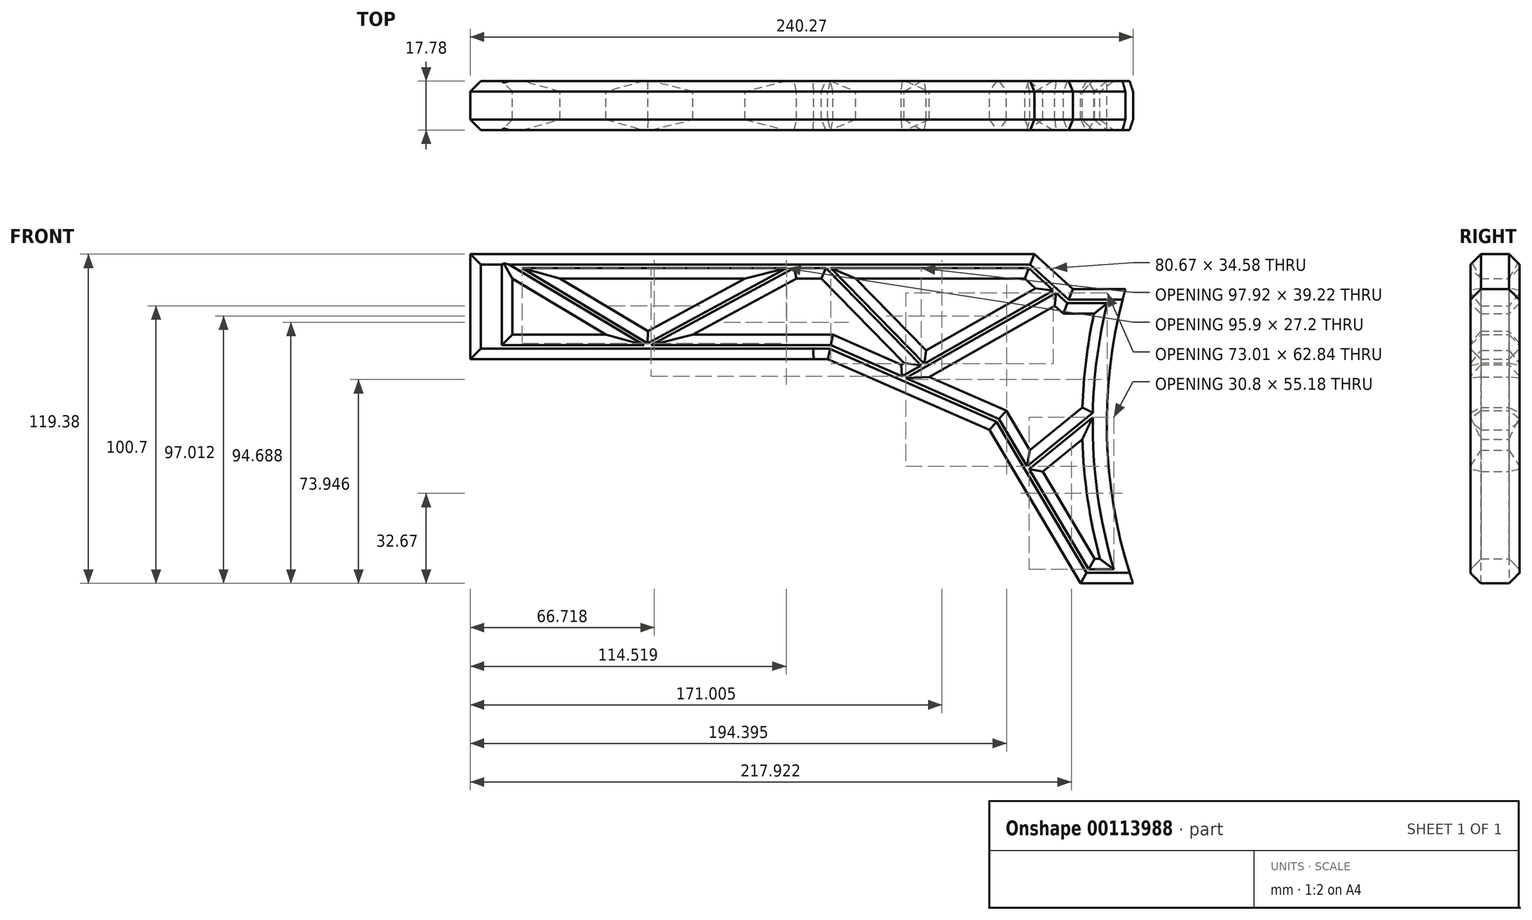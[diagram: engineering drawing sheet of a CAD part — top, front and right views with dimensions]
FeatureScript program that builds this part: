
annotation { "Feature Type Name" : "Feature", "Feature Type Description" : "" }
export const myFeature = defineFeature(function(context is Context, id is Id, definition is map)
    precondition{}
    {
        {
            var Q0;
            Q0=qCreatedBy(makeId("Front.planeOp"),FACE);
            var sketch = newSketch(context, id + "F0", { "sketchPlane" : qUnion([Q0])});
            skLineSegment(sketch, "E0", {"start": v(16.5, 0) * mm, "end": v(146.11, 0) * mm});
            skLineSegment(sketch, "E1", {"start": v(16.5, 38.1) * mm, "end": v(220.98, 38.1) * mm});
            skPoint(sketch, "E2.third.point", {"position": v(702.6, 206.51) * mm});
            skLineSegment(sketch, "E3", {"start": v(106.48, -51.1) * mm, "end": v(103.94, -51.1) * mm});
            skLineSegment(sketch, "E4.trimOffspring", {"start": v(-124.11, 15.8) * mm, "end": v(-124.11, 15.18) * mm, "construction": true});
            skLineSegment(sketch, "E5", {"start": v(220.98, 38.1) * mm, "end": v(234.95, 25.4) * mm});
            skLineSegment(sketch, "E6", {"start": v(234.95, 25.4) * mm, "end": v(254, 25.4) * mm});
            skLineSegment(sketch, "E7", {"start": v(256.78, -81.28) * mm, "end": v(237.73, -81.28) * mm});
            skArc(sketch, "E8", {"start": v(146.11, 0) * mm, "mid": v(143.53, 0.04) * mm, "end": v(140.94, 0) * mm});
            skLineSegment(sketch, "E9", {"start": v(237.73, -81.28) * mm, "end": v(204.68, -25.64) * mm});
            skLineSegment(sketch, "E10", {"start": v(204.68, -25.64) * mm, "end": v(146.11, 0) * mm});
            skArc(sketch, "E11", {"start": v(254, 25.4) * mm, "mid": v(247.3, -28.15) * mm, "end": v(256.78, -81.28) * mm});
            skLineSegment(sketch, "E12.2", {"start": v(31.75, 8.9) * mm, "end": v(48.98, 8.9) * mm});
            skLineSegment(sketch, "E12.3", {"start": v(217.54, 29.2) * mm, "end": v(221.4, 25.7) * mm});
            skLineSegment(sketch, "E12.4", {"start": v(210.86, -18.65) * mm, "end": v(182.89, -6.4) * mm});
            skLineSegment(sketch, "E12.5", {"start": v(242.79, -72.4) * mm, "end": v(223.99, -40.74) * mm});
            skArc(sketch, "E12.6", {"start": v(242.62, 16.5) * mm, "mid": v(239.75, -0.4) * mm, "end": v(238.43, -17.5) * mm});
            skLineSegment(sketch, "E12.7", {"start": v(231.51, 16.5) * mm, "end": v(242.62, 16.5) * mm});
            skLineSegment(sketch, "E13", {"start": v(242.79, -72.4) * mm, "end": v(244.8, -72.4) * mm});
            skLineSegment(sketch, "E14", {"start": v(219.4, -33.01) * mm, "end": v(238.43, -17.5) * mm});
            skLineSegment(sketch, "E15", {"start": v(223.99, -40.74) * mm, "end": v(238.42, -28.98) * mm});
            skLineSegment(sketch, "E16.trimOffspring", {"start": v(219.4, -33.01) * mm, "end": v(210.86, -18.65) * mm});
            skArc(sketch, "E17.trimOffspring", {"start": v(238.42, -28.98) * mm, "mid": v(240.34, -50.87) * mm, "end": v(244.8, -72.39) * mm});
            skLineSegment(sketch, "E18", {"start": v(221.4, 25.7) * mm, "end": v(181.8, 3.2) * mm});
            skLineSegment(sketch, "E19", {"start": v(182.89, -6.4) * mm, "end": v(228.32, 19.41) * mm});
            skLineSegment(sketch, "E20", {"start": v(173.8, -1.34) * mm, "end": v(143.8, 29.2) * mm});
            skLineSegment(sketch, "E21", {"start": v(156.26, 29.21) * mm, "end": v(181.8, 3.2) * mm});
            skLineSegment(sketch, "E22.trimOffspring", {"start": v(173.8, -1.34) * mm, "end": v(172.73, -1.95) * mm});
            skLineSegment(sketch, "E23.trimOffspring", {"start": v(172.73, -1.95) * mm, "end": v(147.98, 8.9) * mm});
            skLineSegment(sketch, "E24.trimOffspring", {"start": v(228.32, 19.41) * mm, "end": v(231.51, 16.5) * mm});
            skLineSegment(sketch, "E25.trimOffspring", {"start": v(156.26, 29.2) * mm, "end": v(217.54, 29.2) * mm});
            skLineSegment(sketch, "E26", {"start": v(134.82, 29.2) * mm, "end": v(97.15, 8.89) * mm});
            skLineSegment(sketch, "E27", {"start": v(80.86, 10.2) * mm, "end": v(116.1, 29.2) * mm});
            skLineSegment(sketch, "E28.trimOffspring", {"start": v(49.07, 29.2) * mm, "end": v(116.1, 29.2) * mm});
            skLineSegment(sketch, "E29.trimOffspring", {"start": v(134.82, 29.2) * mm, "end": v(143.8, 29.2) * mm});
            skLineSegment(sketch, "E30.trimOffspring", {"start": v(97.15, 8.9) * mm, "end": v(147.98, 8.9) * mm});
            skLineSegment(sketch, "E31", {"start": v(16.51, 29.21) * mm, "end": v(16.51, 8.9) * mm});
            skPoint(sketch, "E32.orphan", {"position": v(8.9, 8.9) * mm});
            skPoint(sketch, "E12.1.start.orphan", {"position": v(8.9, 29.21) * mm});
            skLineSegment(sketch, "E33", {"start": v(16.5, 38.1) * mm, "end": v(16.5, 0) * mm});
            skPoint(sketch, "E34.start.orphan", {"position": v(0, 38.1) * mm});
            skPoint(sketch, "E35.orphan", {"position": v(0, 0) * mm});
            skLineSegment(sketch, "E36", {"start": v(48.98, 8.89) * mm, "end": v(65.73, 8.89) * mm});
            skLineSegment(sketch, "E37", {"start": v(31.75, 29.21) * mm, "end": v(31.75, 8.9) * mm});
            skLineSegment(sketch, "E38", {"start": v(31.75, 29.21) * mm, "end": v(65.73, 8.89) * mm});
            skLineSegment(sketch, "E39", {"start": v(49.07, 29.2) * mm, "end": v(80.86, 10.2) * mm});
            skPoint(sketch, "E40.end.orphan", {"position": v(33.27, 29.2) * mm});
            skPoint(sketch, "E41.orphan", {"position": v(78.43, 8.9) * mm});
            skSolve(sketch);
        }
        {
            var Q0;
            Q0=makeQuery(id+"F0.imprint","IMPRINT",FACE,{"disambiguationData":[TD([[makeQuery(id+"F0.imprint","IMPRINT",EDGE,{"derivedFrom":sQuery(id+"F0.wireOp",EDGE,"E1")}),-1.0]])]});
            extrude(context, id + "F1", {"entities" : qUnion([Q0]), "depth" : 17.78 * mm});
        }
        {
            var Q0;
            Q0=makeQuery(id+"F1.opExtrude","CAP_EDGE",EDGE,{"disambiguationData":[OSD([sQuery(id+"F0.wireOp",EDGE,"E8")])],"isStart":false});
            var Q1;
            Q1=makeQuery(id+"F1.opExtrude","CAP_EDGE",EDGE,{"disambiguationData":[OSD([sQuery(id+"F0.wireOp",EDGE,"E10")])],"isStart":false});
            var Q2;
            Q2=makeQuery(id+"F1.opExtrude","CAP_EDGE",EDGE,{"disambiguationData":[OSD([sQuery(id+"F0.wireOp",EDGE,"E9")])],"isStart":false});
            var Q3;
            Q3=makeQuery(id+"F1.opExtrude","CAP_EDGE",EDGE,{"disambiguationData":[OSD([sQuery(id+"F0.wireOp",EDGE,"E7")])],"isStart":false});
            var Q4;
            Q4=makeQuery(id+"F1.opExtrude","CAP_EDGE",EDGE,{"disambiguationData":[OSD([sQuery(id+"F0.wireOp",EDGE,"E17.trimOffspring")])],"isStart":false});
            var Q5;
            Q5=makeQuery(id+"F1.opExtrude","CAP_EDGE",EDGE,{"disambiguationData":[OSD([sQuery(id+"F0.wireOp",EDGE,"E12.5")])],"isStart":false});
            var Q6;
            Q6=makeQuery(id+"F1.opExtrude","CAP_EDGE",EDGE,{"disambiguationData":[OSD([sQuery(id+"F0.wireOp",EDGE,"E13")])],"isStart":false});
            var Q7;
            Q7=makeQuery(id+"F1.opExtrude","CAP_EDGE",EDGE,{"disambiguationData":[OSD([sQuery(id+"F0.wireOp",EDGE,"E15")])],"isStart":false});
            var Q8;
            Q8=makeQuery(id+"F1.opExtrude","CAP_EDGE",EDGE,{"disambiguationData":[OSD([sQuery(id+"F0.wireOp",EDGE,"E16.trimOffspring")])],"isStart":false});
            var Q9;
            Q9=makeQuery(id+"F1.opExtrude","CAP_EDGE",EDGE,{"disambiguationData":[OSD([sQuery(id+"F0.wireOp",EDGE,"E14")])],"isStart":false});
            var Q10;
            Q10=makeQuery(id+"F1.opExtrude","CAP_EDGE",EDGE,{"disambiguationData":[OSD([sQuery(id+"F0.wireOp",EDGE,"E12.6")])],"isStart":false});
            var Q11;
            Q11=makeQuery(id+"F1.opExtrude","CAP_EDGE",EDGE,{"disambiguationData":[OSD([sQuery(id+"F0.wireOp",EDGE,"E12.7")])],"isStart":false});
            var Q12;
            Q12=makeQuery(id+"F1.opExtrude","CAP_EDGE",EDGE,{"disambiguationData":[OSD([sQuery(id+"F0.wireOp",EDGE,"E24.trimOffspring")])],"isStart":false});
            var Q13;
            Q13=makeQuery(id+"F1.opExtrude","CAP_EDGE",EDGE,{"disambiguationData":[OSD([sQuery(id+"F0.wireOp",EDGE,"E19")])],"isStart":false});
            var Q14;
            Q14=makeQuery(id+"F1.opExtrude","CAP_EDGE",EDGE,{"disambiguationData":[OSD([sQuery(id+"F0.wireOp",EDGE,"E12.4")])],"isStart":false});
            var Q15;
            Q15=makeQuery(id+"F1.opExtrude","CAP_EDGE",EDGE,{"disambiguationData":[OSD([sQuery(id+"F0.wireOp",EDGE,"E12.3")])],"isStart":false});
            var Q16;
            Q16=makeQuery(id+"F1.opExtrude","CAP_EDGE",EDGE,{"disambiguationData":[OSD([sQuery(id+"F0.wireOp",EDGE,"E25.trimOffspring")])],"isStart":false});
            var Q17;
            Q17=makeQuery(id+"F1.opExtrude","CAP_EDGE",EDGE,{"disambiguationData":[OSD([sQuery(id+"F0.wireOp",EDGE,"E21")])],"isStart":false});
            var Q18;
            Q18=makeQuery(id+"F1.opExtrude","CAP_EDGE",EDGE,{"disambiguationData":[OSD([sQuery(id+"F0.wireOp",EDGE,"E18")])],"isStart":false});
            var Q19;
            Q19=makeQuery(id+"F1.opExtrude","CAP_EDGE",EDGE,{"disambiguationData":[OSD([sQuery(id+"F0.wireOp",EDGE,"E23.trimOffspring")])],"isStart":false});
            var Q20;
            Q20=makeQuery(id+"F1.opExtrude","CAP_EDGE",EDGE,{"disambiguationData":[OSD([sQuery(id+"F0.wireOp",EDGE,"E30.trimOffspring")])],"isStart":false});
            var Q21;
            Q21=makeQuery(id+"F1.opExtrude","CAP_EDGE",EDGE,{"disambiguationData":[OSD([sQuery(id+"F0.wireOp",EDGE,"E22.trimOffspring")])],"isStart":false});
            var Q22;
            Q22=makeQuery(id+"F1.opExtrude","CAP_EDGE",EDGE,{"disambiguationData":[OSD([sQuery(id+"F0.wireOp",EDGE,"E20")])],"isStart":false});
            var Q23;
            Q23=makeQuery(id+"F1.opExtrude","CAP_EDGE",EDGE,{"disambiguationData":[OSD([sQuery(id+"F0.wireOp",EDGE,"E29.trimOffspring")])],"isStart":false});
            var Q24;
            Q24=makeQuery(id+"F1.opExtrude","CAP_EDGE",EDGE,{"disambiguationData":[OSD([sQuery(id+"F0.wireOp",EDGE,"E26")])],"isStart":false});
            var Q25;
            Q25=makeQuery(id+"F1.opExtrude","CAP_EDGE",EDGE,{"disambiguationData":[OSD([sQuery(id+"F0.wireOp",EDGE,"8kjQfZER-0lHH-HhN7-aV4i-Qcd4DPzWzpJs")])],"isStart":false});
            var Q26;
            Q26=makeQuery(id+"F1.opExtrude","CAP_EDGE",EDGE,{"disambiguationData":[OSD([sQuery(id+"F0.wireOp",EDGE,"E28.trimOffspring")])],"isStart":false});
            var Q27;
            Q27=makeQuery(id+"F1.opExtrude","CAP_EDGE",EDGE,{"disambiguationData":[OSD([sQuery(id+"F0.wireOp",EDGE,"E27")])],"isStart":false});
            var Q28;
            Q28=makeQuery(id+"F1.opExtrude","CAP_EDGE",EDGE,{"disambiguationData":[OSD([sQuery(id+"F0.wireOp",EDGE,"9419f677-d06b-4c3d-bac2-6876a50477b4.trimOffspring")])],"isStart":false});
            var Q29;
            Q29=makeQuery(id+"F1.opExtrude","CAP_EDGE",EDGE,{"disambiguationData":[OSD([sQuery(id+"F0.wireOp",EDGE,"E12.2")])],"isStart":false});
            var Q30;
            Q30=makeQuery(id+"F1.opExtrude","CAP_EDGE",EDGE,{"disambiguationData":[OSD([sQuery(id+"F0.wireOp",EDGE,"G8ACPXqJ-KlJt-v5ie-DtNp-ziiiNlemSXnz")])],"isStart":false});
            var Q31;
            Q31=makeQuery(id+"F1.opExtrude","CAP_EDGE",EDGE,{"disambiguationData":[OSD([sQuery(id+"F0.wireOp",EDGE,"E31")])],"isStart":false});
            var Q32;
            Q32=makeQuery(id+"F1.opExtrude","CAP_EDGE",EDGE,{"disambiguationData":[OSD([sQuery(id+"F0.wireOp",EDGE,"E1")])],"isStart":false});
            var Q33;
            Q33=makeQuery(id+"F1.opExtrude","CAP_EDGE",EDGE,{"disambiguationData":[OSD([sQuery(id+"F0.wireOp",EDGE,"E5")])],"isStart":true});
            var Q34;
            Q34=makeQuery(id+"F1.opExtrude","CAP_EDGE",EDGE,{"disambiguationData":[OSD([sQuery(id+"F0.wireOp",EDGE,"E6")])],"isStart":false});
            var Q35;
            Q35=makeQuery(id+"F1.opExtrude","CAP_EDGE",EDGE,{"disambiguationData":[OSD([sQuery(id+"F0.wireOp",EDGE,"E5")])],"isStart":false});
            var Q36;
            Q36=makeQuery(id+"F1.opExtrude","CAP_EDGE",EDGE,{"disambiguationData":[OSD([sQuery(id+"F0.wireOp",EDGE,"E0")])],"isStart":false});
            var Q37;
            Q37=makeQuery(id+"F1.opExtrude","CAP_EDGE",EDGE,{"disambiguationData":[OSD([sQuery(id+"F0.wireOp",EDGE,"E12.2")])],"isStart":true});
            var Q38;
            Q38=makeQuery(id+"F1.opExtrude","CAP_EDGE",EDGE,{"disambiguationData":[OSD([sQuery(id+"F0.wireOp",EDGE,"G8ACPXqJ-KlJt-v5ie-DtNp-ziiiNlemSXnz")])],"isStart":true});
            var Q39;
            Q39=makeQuery(id+"F1.opExtrude","CAP_EDGE",EDGE,{"disambiguationData":[OSD([sQuery(id+"F0.wireOp",EDGE,"9419f677-d06b-4c3d-bac2-6876a50477b4.trimOffspring")])],"isStart":true});
            var Q40;
            Q40=makeQuery(id+"F1.opExtrude","CAP_EDGE",EDGE,{"disambiguationData":[OSD([sQuery(id+"F0.wireOp",EDGE,"8kjQfZER-0lHH-HhN7-aV4i-Qcd4DPzWzpJs")])],"isStart":true});
            var Q41;
            Q41=makeQuery(id+"F1.opExtrude","CAP_EDGE",EDGE,{"disambiguationData":[OSD([sQuery(id+"F0.wireOp",EDGE,"E27")])],"isStart":true});
            var Q42;
            Q42=makeQuery(id+"F1.opExtrude","CAP_EDGE",EDGE,{"disambiguationData":[OSD([sQuery(id+"F0.wireOp",EDGE,"E31")])],"isStart":true});
            var Q43;
            Q43=makeQuery(id+"F1.opExtrude","CAP_EDGE",EDGE,{"disambiguationData":[OSD([sQuery(id+"F0.wireOp",EDGE,"E29.trimOffspring")])],"isStart":true});
            var Q44;
            Q44=makeQuery(id+"F1.opExtrude","CAP_EDGE",EDGE,{"disambiguationData":[OSD([sQuery(id+"F0.wireOp",EDGE,"E26")])],"isStart":true});
            var Q45;
            Q45=makeQuery(id+"F1.opExtrude","CAP_EDGE",EDGE,{"disambiguationData":[OSD([sQuery(id+"F0.wireOp",EDGE,"E28.trimOffspring")])],"isStart":true});
            var Q46;
            Q46=makeQuery(id+"F1.opExtrude","CAP_EDGE",EDGE,{"disambiguationData":[OSD([sQuery(id+"F0.wireOp",EDGE,"E22.trimOffspring")])],"isStart":true});
            var Q47;
            Q47=makeQuery(id+"F1.opExtrude","CAP_EDGE",EDGE,{"disambiguationData":[OSD([sQuery(id+"F0.wireOp",EDGE,"E20")])],"isStart":true});
            var Q48;
            Q48=makeQuery(id+"F1.opExtrude","CAP_EDGE",EDGE,{"disambiguationData":[OSD([sQuery(id+"F0.wireOp",EDGE,"E23.trimOffspring")])],"isStart":true});
            var Q49;
            Q49=makeQuery(id+"F1.opExtrude","CAP_EDGE",EDGE,{"disambiguationData":[OSD([sQuery(id+"F0.wireOp",EDGE,"E18")])],"isStart":true});
            var Q50;
            Q50=makeQuery(id+"F1.opExtrude","CAP_EDGE",EDGE,{"disambiguationData":[OSD([sQuery(id+"F0.wireOp",EDGE,"E14")])],"isStart":true});
            var Q51;
            Q51=makeQuery(id+"F1.opExtrude","CAP_EDGE",EDGE,{"disambiguationData":[OSD([sQuery(id+"F0.wireOp",EDGE,"E30.trimOffspring")])],"isStart":true});
            var Q52;
            Q52=makeQuery(id+"F1.opExtrude","CAP_EDGE",EDGE,{"disambiguationData":[OSD([sQuery(id+"F0.wireOp",EDGE,"E12.4")])],"isStart":true});
            var Q53;
            Q53=makeQuery(id+"F1.opExtrude","CAP_EDGE",EDGE,{"disambiguationData":[OSD([sQuery(id+"F0.wireOp",EDGE,"E16.trimOffspring")])],"isStart":true});
            var Q54;
            Q54=makeQuery(id+"F1.opExtrude","CAP_EDGE",EDGE,{"disambiguationData":[OSD([sQuery(id+"F0.wireOp",EDGE,"E21")])],"isStart":true});
            var Q55;
            Q55=makeQuery(id+"F1.opExtrude","CAP_EDGE",EDGE,{"disambiguationData":[OSD([sQuery(id+"F0.wireOp",EDGE,"E12.3")])],"isStart":true});
            var Q56;
            Q56=makeQuery(id+"F1.opExtrude","CAP_EDGE",EDGE,{"disambiguationData":[OSD([sQuery(id+"F0.wireOp",EDGE,"E25.trimOffspring")])],"isStart":true});
            var Q57;
            Q57=makeQuery(id+"F1.opExtrude","CAP_EDGE",EDGE,{"disambiguationData":[OSD([sQuery(id+"F0.wireOp",EDGE,"E24.trimOffspring")])],"isStart":true});
            var Q58;
            Q58=makeQuery(id+"F1.opExtrude","CAP_EDGE",EDGE,{"disambiguationData":[OSD([sQuery(id+"F0.wireOp",EDGE,"E19")])],"isStart":true});
            var Q59;
            Q59=makeQuery(id+"F1.opExtrude","CAP_EDGE",EDGE,{"disambiguationData":[OSD([sQuery(id+"F0.wireOp",EDGE,"E12.7")])],"isStart":true});
            var Q60;
            Q60=makeQuery(id+"F1.opExtrude","CAP_EDGE",EDGE,{"disambiguationData":[OSD([sQuery(id+"F0.wireOp",EDGE,"E12.6")])],"isStart":true});
            var Q61;
            Q61=makeQuery(id+"F1.opExtrude","CAP_EDGE",EDGE,{"disambiguationData":[OSD([sQuery(id+"F0.wireOp",EDGE,"E17.trimOffspring")])],"isStart":true});
            var Q62;
            Q62=makeQuery(id+"F1.opExtrude","CAP_EDGE",EDGE,{"disambiguationData":[OSD([sQuery(id+"F0.wireOp",EDGE,"E15")])],"isStart":true});
            var Q63;
            Q63=makeQuery(id+"F1.opExtrude","CAP_EDGE",EDGE,{"disambiguationData":[OSD([sQuery(id+"F0.wireOp",EDGE,"E13")])],"isStart":true});
            var Q64;
            Q64=makeQuery(id+"F1.opExtrude","CAP_EDGE",EDGE,{"disambiguationData":[OSD([sQuery(id+"F0.wireOp",EDGE,"E12.5")])],"isStart":true});
            var Q65;
            Q65=makeQuery(id+"F1.opExtrude","CAP_EDGE",EDGE,{"disambiguationData":[OSD([sQuery(id+"F0.wireOp",EDGE,"E7")])],"isStart":true});
            var Q66;
            Q66=makeQuery(id+"F1.opExtrude","CAP_EDGE",EDGE,{"disambiguationData":[OSD([sQuery(id+"F0.wireOp",EDGE,"E9")])],"isStart":true});
            var Q67;
            Q67=makeQuery(id+"F1.opExtrude","CAP_EDGE",EDGE,{"disambiguationData":[OSD([sQuery(id+"F0.wireOp",EDGE,"E10")])],"isStart":true});
            var Q68;
            Q68=makeQuery(id+"F1.opExtrude","CAP_EDGE",EDGE,{"disambiguationData":[OSD([sQuery(id+"F0.wireOp",EDGE,"E8")])],"isStart":true});
            var Q69;
            Q69=makeQuery(id+"F1.opExtrude","CAP_EDGE",EDGE,{"disambiguationData":[OSD([sQuery(id+"F0.wireOp",EDGE,"E0")])],"isStart":true});
            var Q70;
            Q70=makeQuery(id+"F1.opExtrude","CAP_EDGE",EDGE,{"disambiguationData":[OSD([sQuery(id+"F0.wireOp",EDGE,"E6")])],"isStart":true});
            var Q71;
            Q71=makeQuery(id+"F1.opExtrude","CAP_EDGE",EDGE,{"disambiguationData":[OSD([sQuery(id+"F0.wireOp",EDGE,"E1")])],"isStart":true});
            var Q72;
            Q72=makeQuery(id+"F1.opExtrude","CAP_EDGE",EDGE,{"disambiguationData":[OSD([sQuery(id+"F0.wireOp",EDGE,"E38")])],"isStart":false});
            var Q73;
            Q73=makeQuery(id+"F1.opExtrude","CAP_EDGE",EDGE,{"disambiguationData":[OSD([sQuery(id+"F0.wireOp",EDGE,"E39")])],"isStart":false});
            var Q74;
            Q74=makeQuery(id+"F1.opExtrude","CAP_EDGE",EDGE,{"disambiguationData":[OSD([sQuery(id+"F0.wireOp",EDGE,"E37")])],"isStart":false});
            var Q75;
            Q75=makeQuery(id+"F1.opExtrude","CAP_EDGE",EDGE,{"disambiguationData":[OSD([sQuery(id+"F0.wireOp",EDGE,"E39")])],"isStart":true});
            var Q76;
            Q76=makeQuery(id+"F1.opExtrude","CAP_EDGE",EDGE,{"disambiguationData":[OSD([sQuery(id+"F0.wireOp",EDGE,"E37")])],"isStart":true});
            var Q77;
            Q77=makeQuery(id+"F1.opExtrude","CAP_EDGE",EDGE,{"disambiguationData":[OSD([sQuery(id+"F0.wireOp",EDGE,"E38")])],"isStart":true});
            chamfer(context, id + "F2", {"entities" : qUnion([Q0, Q1, Q2, Q3, Q4, Q5, Q6, Q7, Q8, Q9, Q10, Q11, Q12, Q13, Q14, Q15, Q16, Q17, Q18, Q19, Q20, Q21, Q22, Q23, Q24, Q25, Q26, Q27, Q28, Q29, Q30, Q31, Q32, Q33, Q34, Q35, Q36, Q37, Q38, Q39, Q40, Q41, Q42, Q43, Q44, Q45, Q46, Q47, Q48, Q49, Q50, Q51, Q52, Q53, Q54, Q55, Q56, Q57, Q58, Q59, Q60, Q61, Q62, Q63, Q64, Q65, Q66, Q67, Q68, Q69, Q70, Q71, Q72, Q73, Q74, Q75, Q76, Q77]), "width" : 3.8 * mm, "tangentPropagation" : true});
        }
    });
